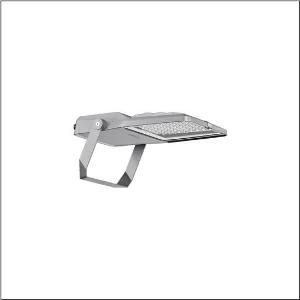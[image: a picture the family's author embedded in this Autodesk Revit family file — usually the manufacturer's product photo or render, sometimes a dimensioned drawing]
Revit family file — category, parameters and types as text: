
# Revit family: floodlight_fl_21_mini___pl64_5xa7775d2e1a_23e2
name_source: partatom
category: Lighting Fixtures
units: mm (PartAtom-declared; Revit-internal decimal feet)

## family parameters
Cut with Voids When Loaded = No
Host = Face
Light Source = No
Part Type = Normal
Room Calculation Point = No
Round Connector Dimension = Use Diameter
Shared = No

## types (1)
- --- (1 x LED, 17220 lm, 142.9 W, 3000K)
    Apparent Load = 143 VA
    CIE Flux Codes = 28 80 98 100 100
    Color Rendering = 70
    Color Temperature = 3000K
    Default Elevation = 1800 mm
    Description = Floodlight FL 21 mini, floodlight, primary light control with lens, of PMMA, primary optical cover: protective disc, of toughened safety glass, transparent, light distribution: PL64, light emission: direct distribution, installation type: surface-mounted, LED, High Power LED, rated luminous flux: 17.220lm, luminous efficacy: 121lm/W, light colour: 730, colour temperature: 3000K, control: flexible luminous flux parameterisation, time-dependent luminous flux control, constant luminous flux control, overheat protection, presetting dimming logarithmic, with terminal, 6-pole, mains connection: 220..240V, AC, 50/60Hz, start of lifetime: 143W, end of service life: 151W, reduction: 63W, luminaire housing, of diecast aluminium, powder-coated, Siteco® metallic grey (DB 702S), corrosivity category C5 mid according to DIN EN ISO 12944, sealing non-destructively replaceable, mounting bracket, of steel, galvanised, powder-coated, Siteco® metallic grey (DB 702S), Smart Interface above, protection rating (complete): IP66, insulation class (complete): insulation class II (safety insulation), certification: CE, ENEC, VDE, protection symbol: D, impact resistance: IK08, permissible operating ambient temperature: -40..+40°C, permissible operating ambient temperature for outdoor applications: -40..+50°C, standard: DIN EN 12944, LABS conformity tested according to VDMA 24364:2018-05, packaging unit: 1 piece

Light Distribution: PL64
    Height = 70 mm
    Lamp = 1 x LED
    Lamp Light Flux = 17220 lm
    Lamp Power = 142.9 W
    Lamp count = 1
    Length = 485 mm
    Luminous efficacy = 121 lm/W
    Manufacturer = Siteco
    ModVariant = No
    Model = 5XA7775D2E1A
    Number of Poles = 1
    OnlyDefault = Yes
    Power Factor = 1
    Product Name = Floodlight FL 21 mini | PL64
    Product group = floodlight | pylon annexe
    ProductGroupID = 6200
    Protection Class = Protection class II
    Protection Degree = IP 66
    RLX_Detail_Level = 1
    RLX_Emergency_Light_Flux = 0 lm
    RLX_Emergency_Type = 0
    RLX_Emergency_Type_DB = No
    RlxData = <blob elided: 96253 chars, md5=9614bf9b>
    Socket = socket
    Standby Power = 0 W
    System Light Flux = 17220 lm
    System Power = 143 W
    Type Comments = factory setting: luminous flux: 100 % | dim-lin: 254 | 730 mA
    Type Image = l_1006845.jpg
    URL = http://relux.com
    VarID = @adj_115463
    Voltage = 0 V
    Weight = 0.00 kg
    Width = 337 mm

## geometry (parser evidence)
native form markers: Blend x4, Sweep x14
no freeform markers — native parametric forms only
